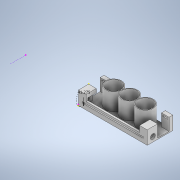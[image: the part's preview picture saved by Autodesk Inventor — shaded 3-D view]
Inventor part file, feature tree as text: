
AUTODESK INVENTOR PART (.ipt)
format: ipt  version: 2020 (Build 240168000, 168)  size: 558,592 bytes
history: native  units: mm
features: sketch x26, extrude x17, fillet x1
ambient origin geometry x8: Origin, YZ Plane, XZ Plane, XY Plane, X Axis, Y Axis, Z Axis, Center Point
bodies: Solid1 (feature_tree)
feature tree (44):
  extrude  "Extrusion1"  Depth=27.0mm
  extrude  "Extrusion2"  Depth=25.0mm
  sketch  "Sketch3"  dims[d4=10.0mm d5=0.0mm d6=10.0mm]
  sketch  "Sketch4"  dims[d7=10.0mm d8=0.0mm d9=5.0mm]
  sketch  "Sketch5"  dims[d10=11.0mm d11=5.0mm]
  extrude  "Extrusion3"  Depth=10.0mm
  extrude  "Extrusion4"  Depth=5.0mm
  extrude  "Extrusion5"  Depth=5.0mm
  extrude  "Extrusion6"  Depth=10.0mm
  fillet  "Fillet1"  Radius=7.5mm
  extrude  "Extrusion7"  Depth=10.0mm TaperAngle=0.0deg
  sketch  "Sketch11"  dims[d28=3.0mm d29=12.0mm]
  extrude  "Extrusion8"  Depth=2.0mm
  sketch  "Sketch13"  dims[d33=41.275mm d34=7.0mm]
  extrude  "Extrusion9"  Depth=3.0mm
  extrude  "Extrusion10"  Depth=12.0mm
  sketch  "Sketch16"  dims[d41=67.0mm d42=0.0mm d43=38.0mm]
  sketch  "Sketch17"  dims[d44=38.0mm d45=38.0mm]
  extrude  "Extrusion11"  Depth=12.0mm
  sketch  "Sketch19"  dims[d48=10.0mm]
  extrude  "Extrusion12"  Depth=23.5mm TaperAngle=0.0deg
  extrude  "Extrusion13"  Depth=7.0mm
  sketch  "Sketch22"  dims[d52=10.0mm d53=0.0mm]
  extrude  "Extrusion14"  Depth=4.5mm
  extrude  "Extrusion15"  Depth=3.0mm
  extrude  "Extrusion16"  Depth=67.0mm
  extrude  "Extrusion17"  Depth=38.0mm
  sketch  "Sketch1"  dims[d0=35.0mm d1=27.0mm]
  sketch  "Sketch2"  dims[d2=25.0mm d3=12.7mm]
  sketch  "Sketch6"  dims[d12=150.0mm d13=0.0mm d14=10.0mm d15=7.5mm d16=0.0mm]
  sketch  "Sketch7"  dims[d17=10.0mm d18=0.0mm d19=10.0mm d20=0.0mm]
  sketch  "Sketch8"  dims[d21=2.0mm d22=7.0mm]
  sketch  "Sketch9"  dims[d23=14.0mm d24=3.0mm]
  sketch  "Sketch10"  dims[d25=140.0mm d26=0.0mm d27=12.0mm]
  sketch  "Sketch12"  dims[d30=3.0mm d31=23.5mm d32=0.0mm]
  sketch  "Sketch14"  dims[d35=4.5mm d36=0.0mm d37=7.0mm]
  sketch  "Sketch15"  dims[d38=4.5mm d39=0.0mm d40=3.0mm]
  sketch  "Sketch18"  dims[d46=30.0mm d47=0.0mm]
  sketch  "Sketch20"  dims[d49=10.0mm]
  sketch  "Sketch21"  dims[d50=32.0mm d51=0.0mm]
  sketch  "Sketch23"  dims[d54=30.0mm d55=0.0mm]
  sketch  "Sketch24"  dims[d56=38.0mm]
  sketch  "Sketch25"  dims[d57=41.5mm]
  sketch  "Sketch26"  dims[d58=38.0mm d59=38.0mm d60=45.0mm d61=0.0mm d62=5.0mm d63=0.0mm]
